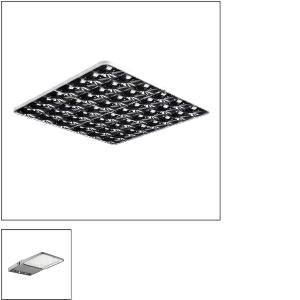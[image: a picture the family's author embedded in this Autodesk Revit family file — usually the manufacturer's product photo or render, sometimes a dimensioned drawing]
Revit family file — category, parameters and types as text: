
# Revit family: siteco_mirrortec_r__indoor___rs05_5nw14093qc_3e65
name_source: partatom
category: Lighting Fixtures
units: mm (PartAtom-declared; Revit-internal decimal feet)

## family parameters
Cut with Voids When Loaded = No
Host = Face
Light Source = No
Part Type = Normal
Room Calculation Point = No
Round Connector Dimension = Use Diameter
Shared = No

## types (1)
- 5XA7682G2H2AC (1 x LED, 33940 lm, 305.7 W, 4000K)
    Apparent Load = 306 VA
    CIE Flux Codes = 47 83 98 53 100
    Color Rendering = 70
    Color Temperature = 4000K
    Default Elevation = 1800 mm
    Description = secondary reflector, for Siteco Mirrortec® Indoor, wire hanger, housing, square, of aluminium, coated, metallic grey (RAL 9006), fresnel reflector 100, of PMMA, aluminized, highly specular, light point resolution, fresnel structure, length: 1.200 mm, width: 1.200 mm

Light Distribution: RS05
    Height = 12 mm  [stored 0.0393701 ft]
    Lamp = 1 x LED
    Lamp Light Flux = 33940 lm
    Lamp Power = 305.7 W
    Lamp count = 1
    Length = 1221 mm
    Luminous efficacy = 111 lm/W
    Manufacturer = Siteco
    ModVariant = No
    Model = 5NW14093QC
    Mounting Place = Ceiling
    Mounting Type = Pendant
    Number of Poles = 1
    OnlyDefault = Yes
    Power Factor = 1
    Product Name = Siteco Mirrortec® Indoor | RS05
    Product group = secondary reflector
    ProductGroupID = 908
    Protection Class = Protection class II
    Protection Degree = IP 66
    RLX_Detail_Level = 1
    RLX_Emergency_Light_Flux = 0 lm
    RLX_Emergency_Type = 0
    RLX_Emergency_Type_DB = No
    RlxData = <blob elided: 123369 chars, md5=f66840d8>
    Socket = socket
    Standby Power = 0 W
    System Light Flux = 33939 lm
    System Power = 306 W
    Type Comments = Floodlight FL 20 midi, floodlight, primary light control with lens, of plastic, primary optical cover: protective disc, of toughened safety glass, transparent, light distribution: RS05, light emission: direct distribution, primary light characteristic: rotationally symmetric, installation type: surface-mounted, LED, High Power LED, rated luminous flux: 38.380lm, luminous efficacy: 126lm/W, light colour: 740, colour temperature: 4000K, control gear: ECG Plus, control: overheat protection, power reduction, digital communication interface, time-dependent luminous flux control, flexible luminous flux parameterisation, electronic power reduction, with terminal, 10-pole, max. 2.5mm², mains connection: 220..240V, AC, 50/60Hz, rated input power: 306W, LED unit, of diecast aluminium, powder-coated, Siteco® metallic grey (DB 702S), corrosivity category C5 mid according to DIN EN ISO 12944, length: 731mm, width: 450mm, height: 76mm, housing frame, of diecast aluminium, powder-coated, Siteco® metallic grey (DB 702S), wall fastening, DALI, protection rating (complete): IP66, insulation class (complete): insulation class II (safety insulation), certification: CE, ENEC, VDE, protection symbol: D, permissible operating ambient temperature: -40..+40°C, permissible operating ambient temperature for outdoor applications: -40..+50°C, standard: DIN EN 12944, packaging unit: 1 piece

individual setting: distance floodlight mirror = 3,5m / reflector tilt = 5°
    Type Image = l_577132_1005944.jpg
    URL = http://relux.com
    VarID = 5xa7682g2h2ac@adj_152917
    Voltage = 0 V
    Weight = 0.00 kg
    Width = 1221 mm

note: [stored X ft] marks values corroborated as IEEE doubles in the binary element streams (Revit-internal decimal feet)

## geometry (parser evidence)
native form markers: Blend x4, Sweep x12
no freeform markers — native parametric forms only
